# Revit family: Drawer Units
name_source: partatom
category: Furniture
revit_build: Autodesk Revit 2018 (Build: 20181011_1500(x64)
units: mm (PartAtom-declared; Revit-internal decimal feet)

## family parameters
Always vertical = Yes
Cut with Voids When Loaded = No
OmniClass Number = 23.40.20.00
OmniClass Title = General Furniture and Specialties
Room Calculation Point = No
Shared = No
Work Plane-Based = No

## types (8) — shared parameters
Carcass_Material = Steel, Mild
Category = LateralFile Drawer Units
Compliance Standards Certification = BS EN 14073 2004 Part 2 & 3, BS EN 14074, BS EN 14074, BS 4875 1998 Part 7 level 4 & Part 8, BS 476 Part 7 1987 Class 2Y
Drawer_Material = Steel, Mild
Expected Life = <10 Years
Finish = Powder Coated
Lock_Material = Steel AISI 4620
Locker Height = 303 mm  [stored 0.994094 ft]
Manufacturer = Bisley
Model = 1
NamePlate_Material = Polypropylene
Range = LateralFile
Revision = V1
Routine Maintenance = We recommend you clean your unit with warm water and a mil detergent solution. A damp cloth can be used to reove dust partles.
Tolerance = 1 mm  [stored 0.00328084 ft]
URL = www.bisley.com
Uniclass 2015 Code = PR_40_30_78_25
Uniclass2015Title = 78 Shelves and Storage Units
Uniclass2015Version = V1.1
Warranty = 10 Years

## per-type parameters (varying)
| type | 3rd Drawer on/off | Carcass | Door_Material | Drawer 1 | Full Dimension | Lock Height | Mid Point Carcass | Top Drawer on/off | Weight |
| 08C20.2HQ | No | Carcasses : 08C20 | Default | Drawers : H 800 | 800mm x 693mm x 470mm | 678 mm  [stored 2.22441 ft] | 400 mm  [stored 1.31234 ft] | No | 74.29 |
| 08C30.3HQ | Yes | Carcasses : 08C30 | <By Category> | Drawers : H 800 | 800mm x 997mm x 470mm | 982 mm  [stored 3.22178 ft] | 400 mm  [stored 1.31234 ft] | No | 94.34kg |
| 08C40.4H | Yes | Carcasses : 08C40 | <By Category> | Drawers : H 800 | 800mm x 1301mm x 470mm | 1286 mm  [stored 4.21916 ft] | 400 mm  [stored 1.31234 ft] | Yes | 86.658kg |
| 09C20.2HQ | No | Carcasses : 09C20.2HQ | <By Category> | Drawers : H 900 | 900mm x 693mm x 470mm | 678 mm  [stored 2.22441 ft] | 450 mm  [stored 1.47638 ft] | No | 81.087kg |
| 09C30.3HQ | Yes | Carcasses : 09C30.3HQ | <By Category> | Drawers : H 900 | 900mm x 997mm x 470mm | 982 mm  [stored 3.22178 ft] | 450 mm  [stored 1.47638 ft] | No | 100.11kg |
| 10C20.2HQ | No | Carcasses : 10C20 | <By Category> | Drawers : H 1000 | 1000mm x 693mm x 470mm | 678 mm  [stored 2.22441 ft] | 500 mm  [stored 1.64042 ft] | No | 88.691kg |
| 10C30.3HQ | Yes | Carcasses : 10C30 | <By Category> | Drawers : H 1000 | 1000mm x 997mm x 470mm | 982 mm  [stored 3.22178 ft] | 500 mm  [stored 1.64042 ft] | No | 114.521kg |
| 10C40.4H | Yes | Carcasses : 10C40 | <By Category> | Drawers : H 1000 | 1000mm x 1301mm x 470mm | 1286 mm  [stored 4.21916 ft] | 500 mm  [stored 1.64042 ft] | Yes | 99.153kg |

note: column(s) folded — value = type name in every type: Model Reference

note: [stored X ft] marks values corroborated as IEEE doubles in the binary element streams (Revit-internal decimal feet)

## geometry (parser evidence)
native form markers: Sweep x31
no freeform markers — native parametric forms only
